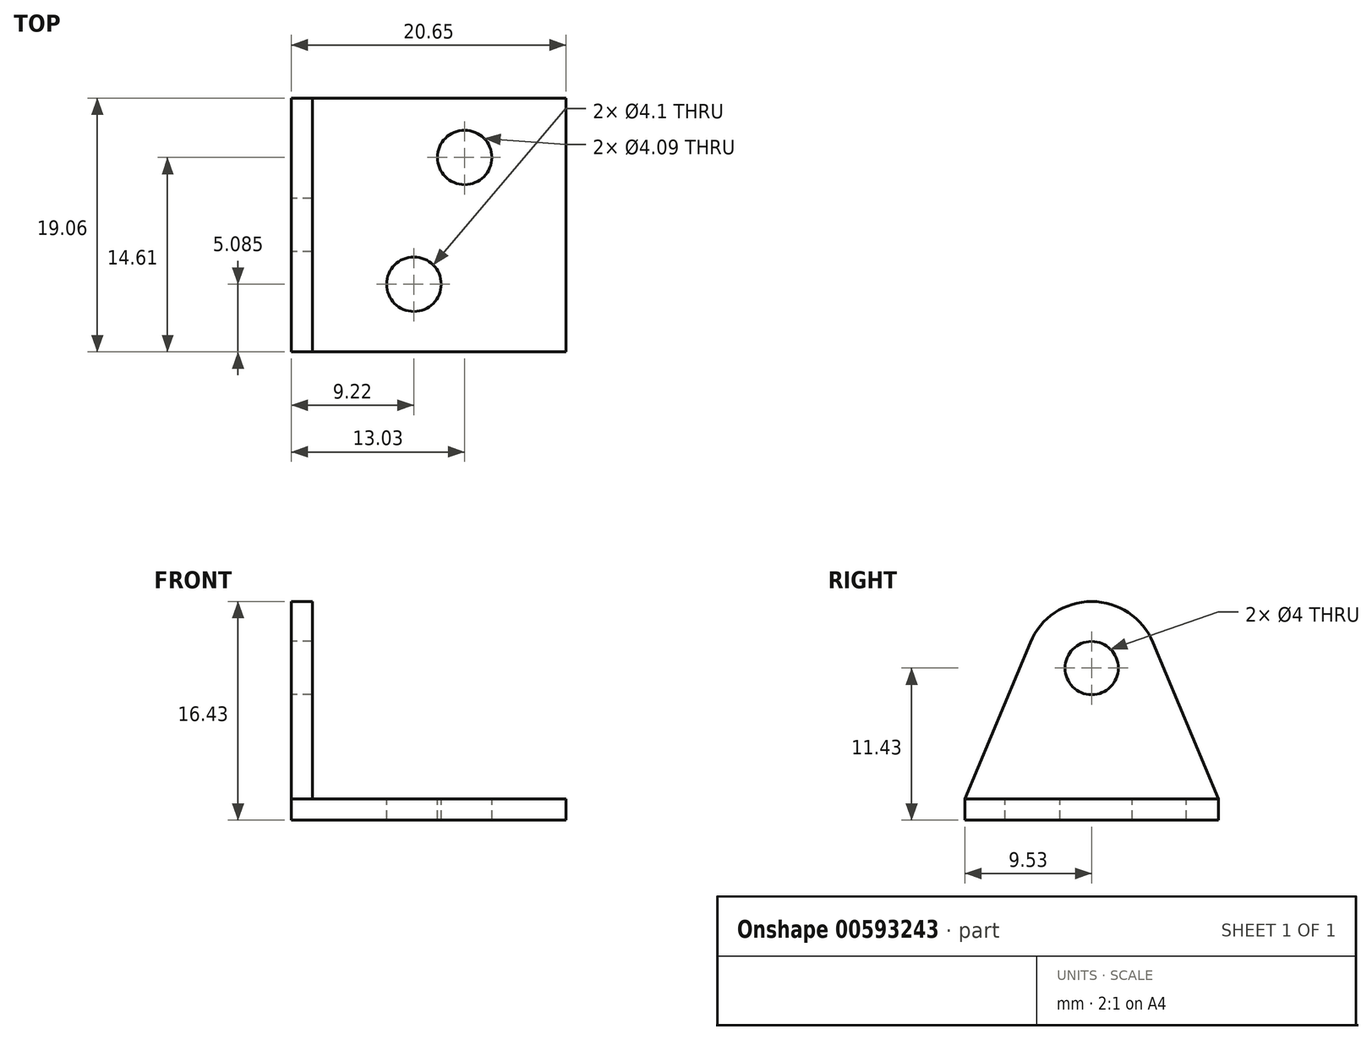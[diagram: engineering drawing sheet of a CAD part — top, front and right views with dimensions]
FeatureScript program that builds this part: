
annotation { "Feature Type Name" : "Feature", "Feature Type Description" : "" }
export const myFeature = defineFeature(function(context is Context, id is Id, definition is map)
    precondition{}
    {
        {
            var Q0;
            Q0=qCreatedBy(makeId("Front.planeOp"),FACE);
            var sketch = newSketch(context, id + "F0", { "sketchPlane" : qUnion([Q0])});
            skLineSegment(sketch, "E0", {"start": v(0, 19.05) * mm, "end": v(0, 0) * mm});
            skLineSegment(sketch, "E1", {"start": v(0, 0) * mm, "end": v(20.65, 0) * mm});
            skLineSegment(sketch, "E2", {"start": v(20.65, 0) * mm, "end": v(20.65, 1.6) * mm});
            skLineSegment(sketch, "E3", {"start": v(20.65, 1.6) * mm, "end": v(1.6, 1.6) * mm});
            skLineSegment(sketch, "E4", {"start": v(1.6, 1.6) * mm, "end": v(1.6, 19.05) * mm});
            skLineSegment(sketch, "E5", {"start": v(1.6, 19.05) * mm, "end": v(0, 19.05) * mm});
            skPoint(sketch, "E6.visualSharp", {"position": v(1.6, 1.6) * mm});
            skSolve(sketch);
        }
        {
            var Q0;
            Q0=qSketchRegion(id+"F0",true);
            extrude(context, id + "F1", {"entities" : qUnion([Q0]), "endBound" : BoundingType.SYMMETRIC, "depth" : 19.05 * mm});
        }
        {
            var Q0;
            Q0=makeQuery(id+"F1.opExtrude","SWEPT_FACE",FACE,{"disambiguationData":[OSD([sQuery(id+"F0.wireOp",EDGE,"E0")])]});
            var sketch = newSketch(context, id + "F2", { "sketchPlane" : qUnion([Q0])});
            skCircle(sketch, "E7", {"center": v(0, 11.43) * mm, "radius": 2 * mm});
            skSolve(sketch);
        }
        {
            var Q0;
            Q0=qSketchRegion(id+"F2",true);
            extrude(context, id + "F3", {"entities" : qUnion([Q0]), "operationType" : NewBodyOperationType.REMOVE, "endBound" : BoundingType.UP_TO_NEXT, "oppositeDirection" : true, "depth" : 25.4 * mm});
        }
        {
            var Q0;
            Q0=makeQuery(id+"F1.opExtrude","SWEPT_FACE",FACE,{"disambiguationData":[OSD([sQuery(id+"F0.wireOp",EDGE,"E0")])]});
            var sketch = newSketch(context, id + "F4", { "sketchPlane" : qUnion([Q0])});
            skLineSegment(sketch, "E8", {"start": v(-9.53, 0) * mm, "end": v(9.53, 0) * mm});
            skLineSegment(sketch, "E9", {"start": v(-4.61, 13.36) * mm, "end": v(-9.53, 1.6) * mm});
            skLineSegment(sketch, "E10", {"start": v(-9.53, 1.6) * mm, "end": v(-9.53, 0) * mm});
            skArc(sketch, "E11", {"start": v(0, 16.43) * mm, "mid": v(-2.77, 15.6) * mm, "end": v(-4.61, 13.36) * mm});
            skLineSegment(sketch, "E12", {"start": v(0, 11.43) * mm, "end": v(0, 12.8) * mm, "construction": true});
            skArc(sketch, "E13.MirrorCS", {"start": v(0, 16.43) * mm, "mid": v(2.77, 15.6) * mm, "end": v(4.61, 13.36) * mm});
            skLineSegment(sketch, "E14.MirrorCS", {"start": v(9.53, 1.6) * mm, "end": v(9.53, 0) * mm});
            skLineSegment(sketch, "E15.MirrorCS", {"start": v(4.61, 13.36) * mm, "end": v(9.53, 1.6) * mm});
            skSolve(sketch);
        }
        {
            var Q0;
            Q0=makeQuery(id+"F4.imprint","IMPRINT",FACE,{"disambiguationData":[TD([[makeQuery(id+"F4.imprint","IMPRINT",EDGE,{"derivedFrom":sQuery(id+"F4.wireOp",EDGE,"O1OHdn4o-TkjY-Bv5V-2hQo-R17gs5ZTKX2j")}),-1.0]])]});
            var Q1;
            {var subQ1=sQuery(id+"F4.wireOp",EDGE,"E9");Q1=makeQuery(id+"F4.imprint","IMPRINT",FACE,{"disambiguationData":[TD([[makeQuery(id+"F4.imprint","IMPRINT",EDGE,{"derivedFrom":subQ1}),-1.0]])]});}
            extrude(context, id + "F5", {"entities" : qUnion([Q0, Q1]), "operationType" : NewBodyOperationType.REMOVE, "endBound" : BoundingType.UP_TO_NEXT, "oppositeDirection" : true, "depth" : 25.4 * mm});
        }
        {
            var Q0;
            Q0=makeQuery(id+"F1.opExtrude","SWEPT_FACE",FACE,{"disambiguationData":[OSD([sQuery(id+"F0.wireOp",EDGE,"E3")])]});
            var sketch = newSketch(context, id + "F6", { "sketchPlane" : qUnion([Q0])});
            skCircle(sketch, "E16", {"center": v(13.03, 5.08) * mm, "radius": 2.04 * mm});
            skCircle(sketch, "E17.MirrorC", {"center": v(9.22, -4.44) * mm, "radius": 2.05 * mm});
            skSolve(sketch);
        }
        {
            var Q0;
            Q0=qSketchRegion(id+"F6",true);
            extrude(context, id + "F7", {"entities" : qUnion([Q0]), "operationType" : NewBodyOperationType.REMOVE, "endBound" : BoundingType.UP_TO_NEXT, "oppositeDirection" : true, "depth" : 25.4 * mm});
        }
    });
